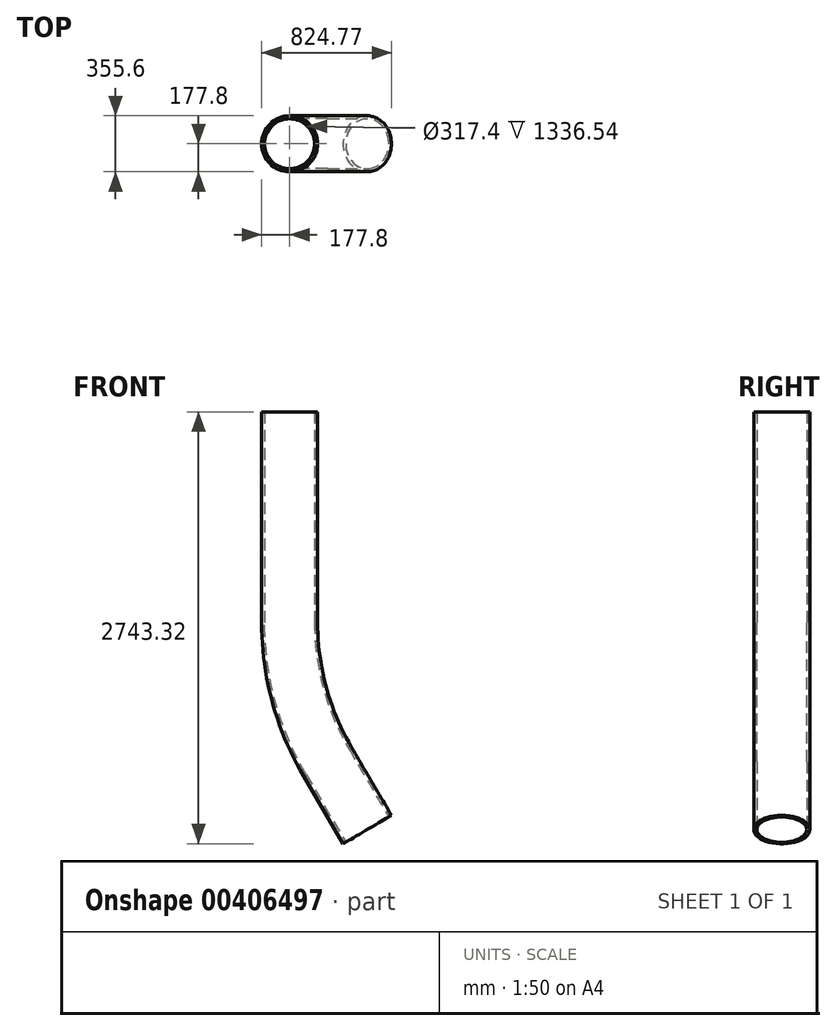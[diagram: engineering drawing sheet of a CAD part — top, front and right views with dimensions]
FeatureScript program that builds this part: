
annotation { "Feature Type Name" : "Feature", "Feature Type Description" : "" }
export const myFeature = defineFeature(function(context is Context, id is Id, definition is map)
    precondition{}
    {
        {
            var Q0;
            Q0=qCreatedBy(makeId("Front.planeOp"),FACE);
            var sketch = newSketch(context, id + "F0", { "sketchPlane" : qUnion([Q0])});
            skLineSegment(sketch, "E0", {"start": v(0, 0) * mm, "end": v(0, 176.35) * mm});
            skSolve(sketch);
        }
        {
            var Q0;
            Q0=qCreatedBy(makeId("Front.planeOp"),FACE);
            var sketch = newSketch(context, id + "F1", { "sketchPlane" : qUnion([Q0])});
            skLineSegment(sketch, "E1", {"start": v(0, 0) * mm, "end": v(0, -1336.54) * mm});
            skLineSegment(sketch, "E2", {"start": v(240.6, -2222.1) * mm, "end": v(493.62, -2653.35) * mm});
            skPoint(sketch, "E3.visualSharp", {"position": v(0, -1812) * mm});
            skArc(sketch, "E3.filletArc", {"start": v(0, -1336.54) * mm, "mid": v(61.22, -1795.37) * mm, "end": v(240.6, -2222.1) * mm});
            skLineSegment(sketch, "E4", {"start": v(0, -1336.54) * mm, "end": v(0, -1812) * mm, "construction": true});
            skLineSegment(sketch, "E5", {"start": v(0, -1812) * mm, "end": v(240.6, -2222.1) * mm, "construction": true});
            skSolve(sketch);
        }
        {
            var Q0;
            Q0=qCreatedBy(makeId("Top.planeOp"),FACE);
            var sketch = newSketch(context, id + "F2", { "sketchPlane" : qUnion([Q0])});
            skCircle(sketch, "E6", {"center": v(0, 0) * mm, "radius": 177.8 * mm});
            skCircle(sketch, "E7", {"center": v(0, 0) * mm, "radius": 158.7 * mm});
            skSolve(sketch);
        }
        {
            var Q0;
            Q0 = qSketchRegion(id + "F2", true);
            var Q1;
            Q1 = qConstructionFilter(qBodyType(qCreatedBy(id + "F1" ,EDGE), BodyType.WIRE), ConstructionObject.NO);
            sweep(context, id + "F3", {"profiles" : qUnion([Q0]), "path" : qUnion([Q1])});
        }
    });
